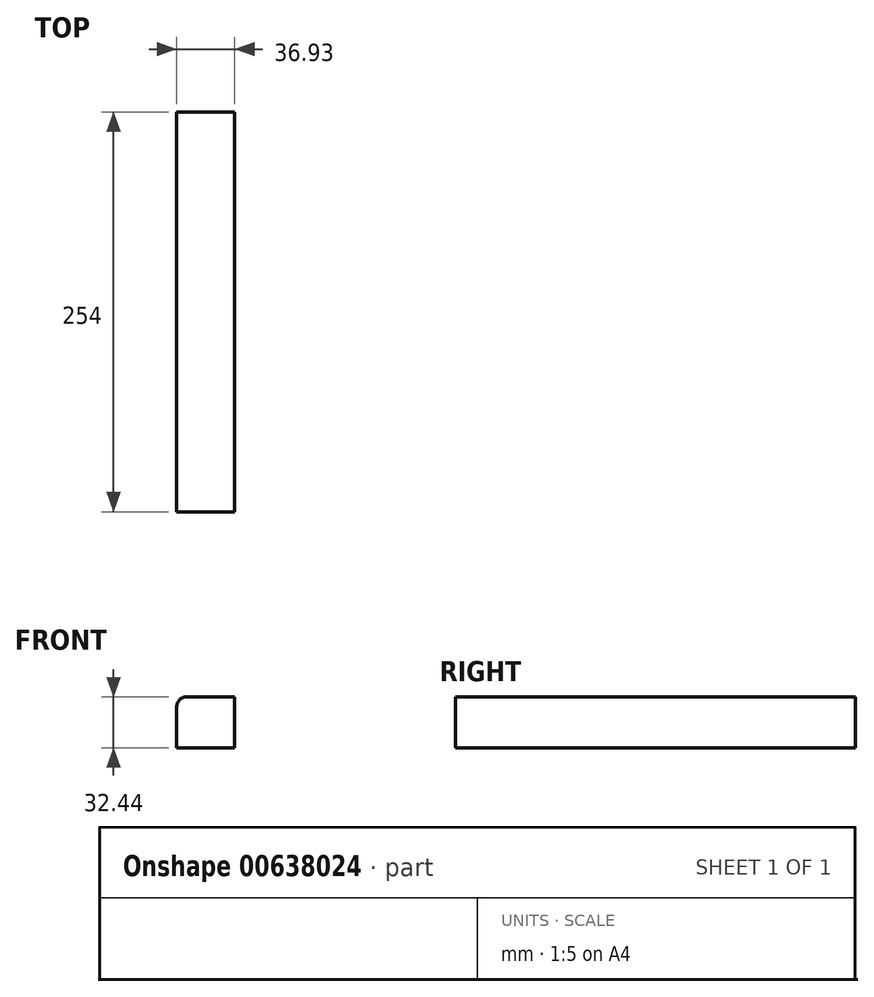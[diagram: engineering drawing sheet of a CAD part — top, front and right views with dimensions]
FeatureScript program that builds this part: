
annotation { "Feature Type Name" : "Feature", "Feature Type Description" : "" }
export const myFeature = defineFeature(function(context is Context, id is Id, definition is map)
    precondition{}
    {
        {
            var Q0;
            Q0=qCreatedBy(makeId("Front.planeOp"),FACE);
            var sketch = newSketch(context, id + "F0", { "sketchPlane" : qUnion([Q0])});
            skLineSegment(sketch, "E0.bottom", {"start": v(0, 0) * mm, "end": v(36.93, 0) * mm});
            skLineSegment(sketch, "E0.top", {"start": v(6.35, 32.44) * mm, "end": v(36.93, 32.44) * mm});
            skLineSegment(sketch, "E0.left", {"start": v(0, 0) * mm, "end": v(0, 26.1) * mm});
            skLineSegment(sketch, "E0.right", {"start": v(36.93, 0) * mm, "end": v(36.93, 32.44) * mm});
            skPoint(sketch, "E1.visualSharp", {"position": v(0, 32.44) * mm});
            skArc(sketch, "E1.filletArc", {"start": v(6.35, 32.44) * mm, "mid": v(1.86, 30.58) * mm, "end": v(0, 26.1) * mm});
            skSolve(sketch);
        }
        {
            var Q0;
            Q0=makeQuery(id+"F0.imprint","IMPRINT",FACE,{"disambiguationData":[TD([[makeQuery(id+"F0.imprint","IMPRINT",EDGE,{"derivedFrom":sQuery(id+"F0.wireOp",EDGE,"E0.bottom")}),1.0]])]});
            extrude(context, id + "F1", {"entities" : qUnion([Q0]), "depth" : 254 * mm, "offsetDistance" : 25.4 * mm});
        }
    });
